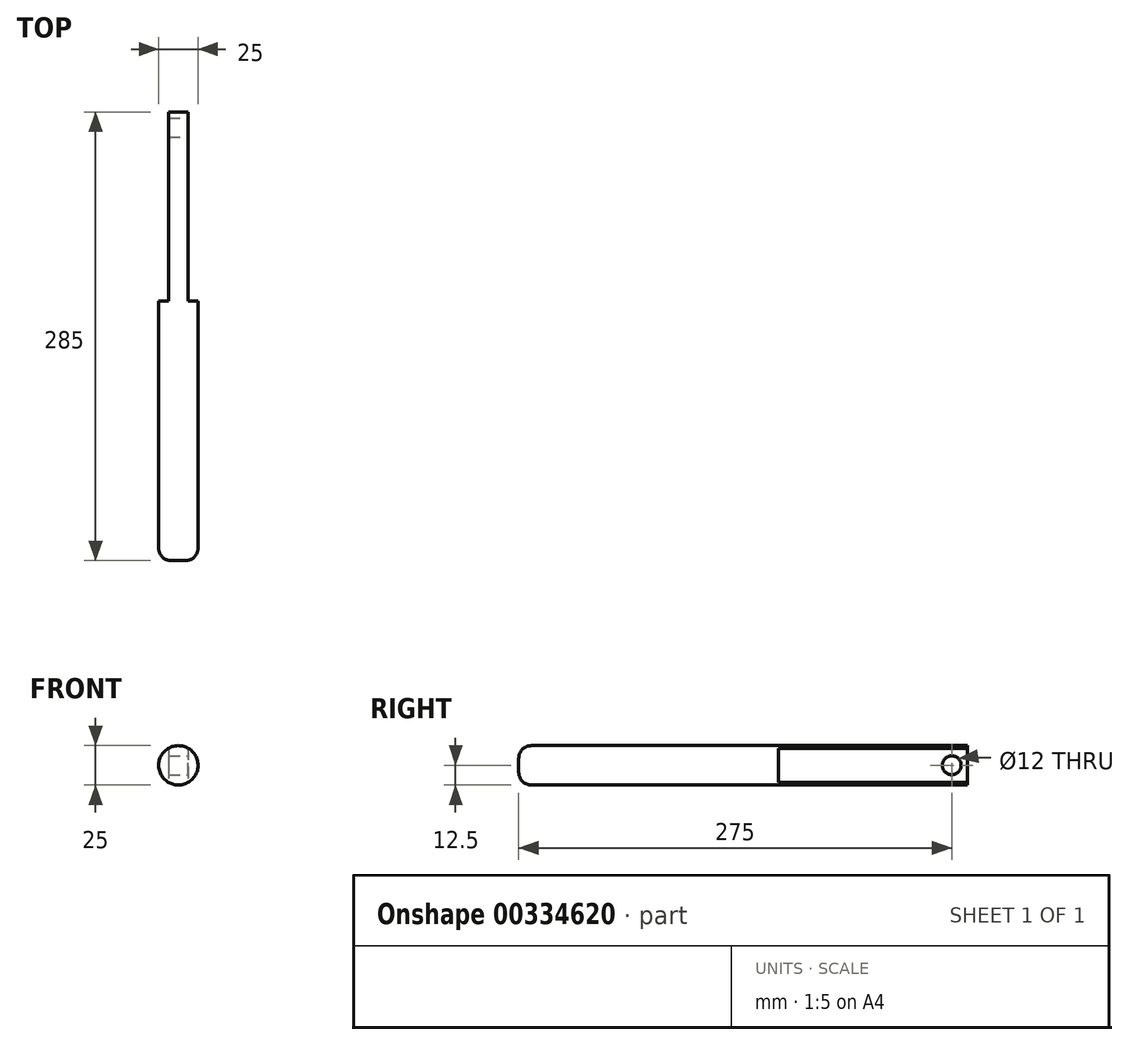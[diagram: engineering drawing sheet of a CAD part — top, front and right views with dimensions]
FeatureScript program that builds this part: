
annotation { "Feature Type Name" : "Feature", "Feature Type Description" : "" }
export const myFeature = defineFeature(function(context is Context, id is Id, definition is map)
    precondition{}
    {
        {
            var Q0;
            Q0=qCreatedBy(makeId("Front.planeOp"),FACE);
            var sketch = newSketch(context, id + "F0", { "sketchPlane" : qUnion([Q0])});
            skCircle(sketch, "E0", {"center": v(0, 0) * mm, "radius": 12.5 * mm});
            skSolve(sketch);
        }
        {
            var Q0;
            Q0 = qSketchRegion(id + "F0", true);
            extrude(context, id + "F1", {"entities" : qUnion([Q0]), "endBound" : BoundingType.SYMMETRIC, "depth" : 165 * mm});
        }
        {
            var Q0;
            Q0=makeQuery(id+"F1.opExtrude","CAP_FACE",FACE,{"disambiguationData":[OSD([sQuery(id+"F0.wireOp",EDGE,"E0")])],"isStart":true});
            var sketch = newSketch(context, id + "F2", { "sketchPlane" : qUnion([Q0])});
            skArc(sketch, "E1", {"start": v(6.25, 10.83) * mm, "mid": v(0, 12.5) * mm, "end": v(-6.25, 10.83) * mm});
            skArc(sketch, "E2.MirrorCS", {"start": v(6.25, -10.83) * mm, "mid": v(0, -12.5) * mm, "end": v(-6.25, -10.83) * mm});
            skLineSegment(sketch, "E3", {"start": v(-6.25, 10.83) * mm, "end": v(-6.25, -10.83) * mm});
            skLineSegment(sketch, "E4", {"start": v(6.25, 10.83) * mm, "end": v(6.25, -10.83) * mm});
            skSolve(sketch);
        }
        {
            var Q0;
            Q0 = qSketchRegion(id + "F2", true);
            extrude(context, id + "F3", {"entities" : qUnion([Q0]), "operationType" : NewBodyOperationType.ADD, "depth" : 120 * mm});
        }
        {
            var Q0;
            Q0=makeQuery(id+"F1.opExtrude","CAP_FACE",FACE,{"disambiguationData":[OSD([sQuery(id+"F0.wireOp",EDGE,"E0")])],"isStart":false});
            fillet(context, id + "F4", {"entities" : qUnion([Q0]), "radius" : 8 * mm, "tangentPropagation" : true, "allowEdgeOverflow" : false});
        }
        {
            var Q0;
            Q0=makeQuery(id+"F3.opExtrude","SWEPT_FACE",FACE,{"disambiguationData":[OSD([sQuery(id+"F2.wireOp",EDGE,"E3")])]});
            var sketch = newSketch(context, id + "F5", { "sketchPlane" : qUnion([Q0])});
            skCircle(sketch, "E5", {"center": v(192.5, 0) * mm, "radius": 6 * mm});
            skSolve(sketch);
        }
        {
            var Q0;
            Q0 = qSketchRegion(id + "F5", true);
            extrude(context, id + "F6", {"entities" : qUnion([Q0]), "operationType" : NewBodyOperationType.REMOVE, "oppositeDirection" : true, "depth" : 25 * mm});
        }
    });
